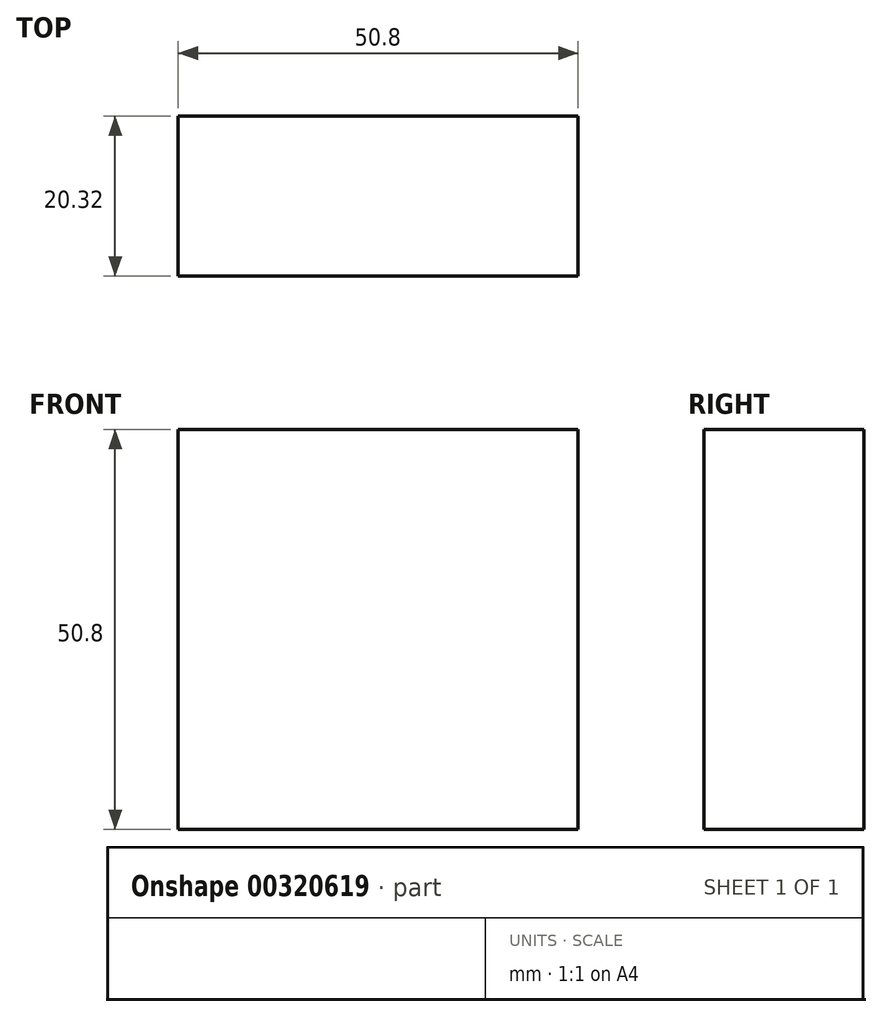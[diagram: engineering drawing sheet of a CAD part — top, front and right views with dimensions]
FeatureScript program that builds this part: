
annotation { "Feature Type Name" : "Feature", "Feature Type Description" : "" }
export const myFeature = defineFeature(function(context is Context, id is Id, definition is map)
    precondition{}
    {
        {
            var Q0;
            Q0=qCreatedBy(makeId("Front.planeOp"),FACE);
            var sketch = newSketch(context, id + "F0", { "sketchPlane" : qUnion([Q0])});
            skLineSegment(sketch, "E0.bottom", {"start": v(-25.4, 25.4) * mm, "end": v(25.4, 25.4) * mm});
            skLineSegment(sketch, "E0.top", {"start": v(-25.4, -25.4) * mm, "end": v(25.4, -25.4) * mm});
            skLineSegment(sketch, "E0.left", {"start": v(-25.4, 25.4) * mm, "end": v(-25.4, -25.4) * mm});
            skLineSegment(sketch, "E0.right", {"start": v(25.4, 25.4) * mm, "end": v(25.4, -25.4) * mm});
            skPoint(sketch, "E0.middle", {"position": v(0, 0) * mm});
            skLineSegment(sketch, "E1.top", {"start": v(70.3, 83.57) * mm, "end": v(19.5, 83.57) * mm});
            skSolve(sketch);
        }
        {
            var Q0;
            Q0 = qSketchRegion(id + "F0", true);
            extrude(context, id + "F1", {"entities" : qUnion([Q0]), "depth" : 20.32 * mm});
        }
    });
